# Revit family: Serene_T&T_Window_F_Standard
name_source: partatom
category: Windows
revit_build: Autodesk Revit 2014 (Build: 20130308_1515(x64)
units: mm (PartAtom-declared; Revit-internal decimal feet)

## types (12) — shared parameters
Area Glazing Sash = 0.43 m²
Centered In Wall = Yes
Custom Sash Height = 1122 mm  [stored 3.6811 ft]
Custom Sash Width = 522 mm  [stored 1.7126 ft]
DG Gasket Finish = Double Glazing Gasket Material
DG Gasket Tickness = 12 mm  [stored 0.0393701 ft]
DG Thickness Calc = 4 mm  [stored 0.0131234 ft]
Default Sill Height = 800 mm  [stored 2.62467 ft]
Description = Tilt and turn window, Type F
Fixed Panel Bottom Width = 510 mm
Frame Thickness = 52 mm
Frame Width = 62 mm  [stored 0.203412 ft]
Length Transom = 510 mm
Limit Fixed Panel Height Max = 1800 mm  [stored 5.90551 ft]
Limit Fixed Panel Height Min = 200 mm  [stored 0.656168 ft]
Limit Fixed Panel Width Max = 1800 mm  [stored 5.90551 ft]
Limit Fixed Panel Width Min = 200 mm  [stored 0.656168 ft]
Limit Sash Height Max = 1500 mm  [stored 4.92126 ft]
Limit Sash Height Min = 300 mm  [stored 0.984252 ft]
Limit Sash Width Max = 700 mm  [stored 2.29659 ft]
Limit Sash Width Min = 300 mm  [stored 0.984252 ft]
Limit Window Height Max = 1880 mm  [stored 6.16798 ft]
Limit Window Height Min = 1430 mm
Limit Window Width Max = 2979 mm
Limit Window Width Min = 1379 mm
Manufacturer = Crealco
Max System DG One Piece Thickness = 4 mm  [stored 0.0131234 ft]
Max System DG Unit Thickness = 20 mm  [stored 0.0656168 ft]
Model = Serene
Mullion Side Spacing = 528 mm  [stored 1.73228 ft]
Sash Edge Gap = 34 mm
Sash Frame Gasket = 3 mm  [stored 0.00984252 ft]
Sash Height = 1122 mm  [stored 3.6811 ft]
Sash Overlap = 28 mm  [stored 0.0918635 ft]
Sash Width = 522 mm  [stored 1.7126 ft]
URL = http://www.crealco.co.za
Wall Closure = By host
zero-valued in all types: Custom Window Exterior Offset

## per-type parameters (varying)
- 52TT-1815SS-1000Pa: Area Glazing Fixed Panel Bottom=0.13 m²; Area Glazing Fixed Panel Middle=0.84 m²; Clearvue Insulated LowE SHGC Value=0.441; Clearvue Insulated LowE U Value=3.78; Clearvue Insulated SHGC Value=0.484; Clearvue Insulated U Value=4.24; Clearvue SHGC Value=0.549; Clearvue U Value=6.2; Custom Windload=1000 mm  [stored 3.28084 ft]; Custom Window Height=1490 mm  [stored 4.88845 ft]; Custom Window Width=1790 mm  [stored 5.8727 ft]; Energy Advantage SHGC Value=0.493; Energy Advantage U Value=5.33; Fixed Panel Bottom Height=260 mm; Fixed Panel Middle Height=1410 mm  [stored 4.62598 ft]; Fixed Panel Middle Width=611 mm; Heavy Duty Mullion=No; Height=1490 mm  [stored 4.88845 ft]; Intruderprufe LowE SHGC Value=0.451; Intruderprufe LowE U Value=4.53; Intruderprufe SHGC Value=0.509; Intruderprufe U Value=6.09; Length Decorative Mullion=1490 mm  [stored 4.88845 ft]; Length Mullion=1410 mm  [stored 4.62598 ft]; Max Pane Area=0.84 m²; Standard Mullion=Yes; Width=1790 mm  [stored 5.8727 ft]; Windload Design=1000 mm  [stored 3.28084 ft]
- 52TT-1815SS-1500Pa: Area Glazing Fixed Panel Bottom=0.13 m²; Area Glazing Fixed Panel Middle=0.84 m²; Clearvue Insulated LowE SHGC Value=0.441; Clearvue Insulated LowE U Value=3.78; Clearvue Insulated SHGC Value=0.484; Clearvue Insulated U Value=4.24; Clearvue SHGC Value=0.549; Clearvue U Value=6.2; Custom Windload=1500 mm  [stored 4.92126 ft]; Custom Window Height=1490 mm  [stored 4.88845 ft]; Custom Window Width=1790 mm  [stored 5.8727 ft]; Energy Advantage SHGC Value=0.493; Energy Advantage U Value=5.33; Fixed Panel Bottom Height=260 mm; Fixed Panel Middle Height=1410 mm  [stored 4.62598 ft]; Fixed Panel Middle Width=611 mm; Heavy Duty Mullion=Yes; Height=1490 mm  [stored 4.88845 ft]; Intruderprufe LowE SHGC Value=0.451; Intruderprufe LowE U Value=4.53; Intruderprufe SHGC Value=0.509; Intruderprufe U Value=6.09; Length Decorative Mullion=1490 mm  [stored 4.88845 ft]; Length Mullion=1410 mm  [stored 4.62598 ft]; Max Pane Area=0.84 m²; Standard Mullion=No; Width=1790 mm  [stored 5.8727 ft]; Windload Design=1500 mm  [stored 4.92126 ft]
- 52TT-1815SS-2000Pa: Area Glazing Fixed Panel Bottom=0.13 m²; Area Glazing Fixed Panel Middle=0.84 m²; Clearvue Insulated LowE SHGC Value=0.441; Clearvue Insulated LowE U Value=3.78; Clearvue Insulated SHGC Value=0.484; Clearvue Insulated U Value=4.24; Clearvue SHGC Value=0.549; Clearvue U Value=6.2; Custom Windload=2000 mm  [stored 6.56168 ft]; Custom Window Height=1490 mm  [stored 4.88845 ft]; Custom Window Width=1790 mm  [stored 5.8727 ft]; Energy Advantage SHGC Value=0.493; Energy Advantage U Value=5.33; Fixed Panel Bottom Height=260 mm; Fixed Panel Middle Height=1410 mm  [stored 4.62598 ft]; Fixed Panel Middle Width=611 mm; Heavy Duty Mullion=Yes; Height=1490 mm  [stored 4.88845 ft]; Intruderprufe LowE SHGC Value=0.451; Intruderprufe LowE U Value=4.53; Intruderprufe SHGC Value=0.509; Intruderprufe U Value=6.09; Length Decorative Mullion=1490 mm  [stored 4.88845 ft]; Length Mullion=1410 mm  [stored 4.62598 ft]; Max Pane Area=0.84 m²; Standard Mullion=No; Width=1790 mm  [stored 5.8727 ft]; Windload Design=2000 mm  [stored 6.56168 ft]
- 52TT-2415SS-1000Pa: Area Glazing Fixed Panel Bottom=0.13 m²; Area Glazing Fixed Panel Middle=1.68 m²; Clearvue Insulated LowE SHGC Value=0.487; Clearvue Insulated LowE U Value=3.42; Clearvue Insulated SHGC Value=0.535; Clearvue Insulated U Value=3.95; Clearvue SHGC Value=0; Clearvue U Value=7.9; Custom Windload=1000 mm  [stored 3.28084 ft]; Custom Window Height=1490 mm  [stored 4.88845 ft]; Custom Window Width=2390 mm  [stored 7.84121 ft]; Energy Advantage SHGC Value=0; Energy Advantage U Value=7.9; Fixed Panel Bottom Height=260 mm; Fixed Panel Middle Height=1410 mm  [stored 4.62598 ft]; Fixed Panel Middle Width=1211 mm; Heavy Duty Mullion=No; Height=1490 mm  [stored 4.88845 ft]; Intruderprufe LowE SHGC Value=0.497; Intruderprufe LowE U Value=4.46; Intruderprufe SHGC Value=0.561; Intruderprufe U Value=6; Length Decorative Mullion=1490 mm  [stored 4.88845 ft]; Length Mullion=1410 mm  [stored 4.62598 ft]; Max Pane Area=1.68 m²; Standard Mullion=Yes; Width=2390 mm  [stored 7.84121 ft]; Windload Design=1000 mm  [stored 3.28084 ft]
- 52TT-2415SS-1500Pa: Area Glazing Fixed Panel Bottom=0.13 m²; Area Glazing Fixed Panel Middle=1.68 m²; Clearvue Insulated LowE SHGC Value=0.487; Clearvue Insulated LowE U Value=3.42; Clearvue Insulated SHGC Value=0.535; Clearvue Insulated U Value=3.95; Clearvue SHGC Value=0; Clearvue U Value=7.9; Custom Windload=1500 mm  [stored 4.92126 ft]; Custom Window Height=1490 mm  [stored 4.88845 ft]; Custom Window Width=2390 mm  [stored 7.84121 ft]; Energy Advantage SHGC Value=0; Energy Advantage U Value=7.9; Fixed Panel Bottom Height=260 mm; Fixed Panel Middle Height=1410 mm  [stored 4.62598 ft]; Fixed Panel Middle Width=1211 mm; Heavy Duty Mullion=Yes; Height=1490 mm  [stored 4.88845 ft]; Intruderprufe LowE SHGC Value=0.497; Intruderprufe LowE U Value=4.46; Intruderprufe SHGC Value=0.561; Intruderprufe U Value=6; Length Decorative Mullion=1490 mm  [stored 4.88845 ft]; Length Mullion=1410 mm  [stored 4.62598 ft]; Max Pane Area=1.68 m²; Standard Mullion=No; Width=2390 mm  [stored 7.84121 ft]; Windload Design=1500 mm  [stored 4.92126 ft]
- 52TT-2415SS-2000Pa: Area Glazing Fixed Panel Bottom=0.13 m²; Area Glazing Fixed Panel Middle=1.68 m²; Clearvue Insulated LowE SHGC Value=0.487; Clearvue Insulated LowE U Value=3.42; Clearvue Insulated SHGC Value=0.535; Clearvue Insulated U Value=3.95; Clearvue SHGC Value=0; Clearvue U Value=7.9; Custom Windload=2000 mm  [stored 6.56168 ft]; Custom Window Height=1490 mm  [stored 4.88845 ft]; Custom Window Width=2390 mm  [stored 7.84121 ft]; Energy Advantage SHGC Value=0; Energy Advantage U Value=7.9; Fixed Panel Bottom Height=260 mm; Fixed Panel Middle Height=1410 mm  [stored 4.62598 ft]; Fixed Panel Middle Width=1211 mm; Heavy Duty Mullion=Yes; Height=1490 mm  [stored 4.88845 ft]; Intruderprufe LowE SHGC Value=0.497; Intruderprufe LowE U Value=4.46; Intruderprufe SHGC Value=0.561; Intruderprufe U Value=6; Length Decorative Mullion=1490 mm  [stored 4.88845 ft]; Length Mullion=1410 mm  [stored 4.62598 ft]; Max Pane Area=1.68 m²; Standard Mullion=No; Width=2390 mm  [stored 7.84121 ft]; Windload Design=2000 mm  [stored 6.56168 ft]
- 52TT-1818SS-1000Pa: Area Glazing Fixed Panel Bottom=0.27 m²; Area Glazing Fixed Panel Middle=1.02 m²; Clearvue Insulated LowE SHGC Value=0.459; Clearvue Insulated LowE U Value=3.64; Clearvue Insulated SHGC Value=0.504; Clearvue Insulated U Value=4.12; Clearvue SHGC Value=0.573; Clearvue U Value=6.16; Custom Windload=1000 mm  [stored 3.28084 ft]; Custom Window Height=1790 mm  [stored 5.8727 ft]; Custom Window Width=1790 mm  [stored 5.8727 ft]; Energy Advantage SHGC Value=0.514; Energy Advantage U Value=5.23; Fixed Panel Bottom Height=560 mm; Fixed Panel Middle Height=1710 mm  [stored 5.61024 ft]; Fixed Panel Middle Width=611 mm; Heavy Duty Mullion=Yes; Height=1790 mm  [stored 5.8727 ft]; Intruderprufe LowE SHGC Value=0.47; Intruderprufe LowE U Value=4.5; Intruderprufe SHGC Value=0.53; Intruderprufe U Value=6.05; Length Decorative Mullion=1790 mm  [stored 5.8727 ft]; Length Mullion=1710 mm  [stored 5.61024 ft]; Max Pane Area=1.02 m²; Standard Mullion=No; Width=1790 mm  [stored 5.8727 ft]; Windload Design=1000 mm  [stored 3.28084 ft]
- 52TT-1818SS-1500Pa: Area Glazing Fixed Panel Bottom=0.27 m²; Area Glazing Fixed Panel Middle=1.02 m²; Clearvue Insulated LowE SHGC Value=0.459; Clearvue Insulated LowE U Value=3.64; Clearvue Insulated SHGC Value=0.504; Clearvue Insulated U Value=4.12; Clearvue SHGC Value=0.573; Clearvue U Value=6.16; Custom Windload=1500 mm  [stored 4.92126 ft]; Custom Window Height=1790 mm  [stored 5.8727 ft]; Custom Window Width=1790 mm  [stored 5.8727 ft]; Energy Advantage SHGC Value=0.514; Energy Advantage U Value=5.23; Fixed Panel Bottom Height=560 mm; Fixed Panel Middle Height=1710 mm  [stored 5.61024 ft]; Fixed Panel Middle Width=611 mm; Heavy Duty Mullion=Yes; Height=1790 mm  [stored 5.8727 ft]; Intruderprufe LowE SHGC Value=0.47; Intruderprufe LowE U Value=4.5; Intruderprufe SHGC Value=0.53; Intruderprufe U Value=6.05; Length Decorative Mullion=1790 mm  [stored 5.8727 ft]; Length Mullion=1710 mm  [stored 5.61024 ft]; Max Pane Area=1.02 m²; Standard Mullion=No; Width=1790 mm  [stored 5.8727 ft]; Windload Design=1500 mm  [stored 4.92126 ft]
- 52TT-1818SS-2000Pa: Area Glazing Fixed Panel Bottom=0.27 m²; Area Glazing Fixed Panel Middle=1.02 m²; Clearvue Insulated LowE SHGC Value=0.459; Clearvue Insulated LowE U Value=3.64; Clearvue Insulated SHGC Value=0.504; Clearvue Insulated U Value=4.12; Clearvue SHGC Value=0.573; Clearvue U Value=6.16; Custom Windload=2000 mm  [stored 6.56168 ft]; Custom Window Height=1790 mm  [stored 5.8727 ft]; Custom Window Width=1790 mm  [stored 5.8727 ft]; Energy Advantage SHGC Value=0.514; Energy Advantage U Value=5.23; Fixed Panel Bottom Height=560 mm; Fixed Panel Middle Height=1710 mm  [stored 5.61024 ft]; Fixed Panel Middle Width=611 mm; Heavy Duty Mullion=Yes; Height=1790 mm  [stored 5.8727 ft]; Intruderprufe LowE SHGC Value=0.47; Intruderprufe LowE U Value=4.5; Intruderprufe SHGC Value=0.53; Intruderprufe U Value=6.05; Length Decorative Mullion=1790 mm  [stored 5.8727 ft]; Length Mullion=1710 mm  [stored 5.61024 ft]; Max Pane Area=1.02 m²; Standard Mullion=No; Width=1790 mm  [stored 5.8727 ft]; Windload Design=2000 mm  [stored 6.56168 ft]
- 52TT-2418SS-1000Pa: Area Glazing Fixed Panel Bottom=0.27 m²; Area Glazing Fixed Panel Middle=2.04 m²; Clearvue Insulated LowE SHGC Value=0.503; Clearvue Insulated LowE U Value=3.29; Clearvue Insulated SHGC Value=0.552; Clearvue Insulated U Value=3.84; Clearvue SHGC Value=0; Clearvue U Value=7.9; Custom Windload=1000 mm  [stored 3.28084 ft]; Custom Window Height=1790 mm  [stored 5.8727 ft]; Custom Window Width=2390 mm  [stored 7.84121 ft]; Energy Advantage SHGC Value=0; Energy Advantage U Value=7.9; Fixed Panel Bottom Height=560 mm; Fixed Panel Middle Height=1710 mm  [stored 5.61024 ft]; Fixed Panel Middle Width=1211 mm; Heavy Duty Mullion=Yes; Height=1790 mm  [stored 5.8727 ft]; Intruderprufe LowE SHGC Value=0.514; Intruderprufe LowE U Value=4.43; Intruderprufe SHGC Value=0.58; Intruderprufe U Value=5.96; Length Decorative Mullion=1790 mm  [stored 5.8727 ft]; Length Mullion=1710 mm  [stored 5.61024 ft]; Max Pane Area=2.04 m²; Standard Mullion=No; Width=2390 mm  [stored 7.84121 ft]; Windload Design=1000 mm  [stored 3.28084 ft]
- 52TT-2418SS-1500Pa: Area Glazing Fixed Panel Bottom=0.27 m²; Area Glazing Fixed Panel Middle=2.04 m²; Clearvue Insulated LowE SHGC Value=0.503; Clearvue Insulated LowE U Value=3.29; Clearvue Insulated SHGC Value=0.552; Clearvue Insulated U Value=3.84; Clearvue SHGC Value=0; Clearvue U Value=7.9; Custom Windload=1500 mm  [stored 4.92126 ft]; Custom Window Height=1790 mm  [stored 5.8727 ft]; Custom Window Width=2390 mm  [stored 7.84121 ft]; Energy Advantage SHGC Value=0; Energy Advantage U Value=7.9; Fixed Panel Bottom Height=560 mm; Fixed Panel Middle Height=1710 mm  [stored 5.61024 ft]; Fixed Panel Middle Width=1211 mm; Heavy Duty Mullion=Yes; Height=1790 mm  [stored 5.8727 ft]; Intruderprufe LowE SHGC Value=0.514; Intruderprufe LowE U Value=4.43; Intruderprufe SHGC Value=0.58; Intruderprufe U Value=5.96; Length Decorative Mullion=1790 mm  [stored 5.8727 ft]; Length Mullion=1710 mm  [stored 5.61024 ft]; Max Pane Area=2.04 m²; Standard Mullion=No; Width=2390 mm  [stored 7.84121 ft]; Windload Design=1500 mm  [stored 4.92126 ft]
- 52TT-2418SS-2000Pa: Area Glazing Fixed Panel Bottom=0.27 m²; Area Glazing Fixed Panel Middle=2.04 m²; Clearvue Insulated LowE SHGC Value=0.503; Clearvue Insulated LowE U Value=3.29; Clearvue Insulated SHGC Value=0.552; Clearvue Insulated U Value=3.84; Clearvue SHGC Value=0; Clearvue U Value=7.9; Custom Windload=2000 mm  [stored 6.56168 ft]; Custom Window Height=1790 mm  [stored 5.8727 ft]; Custom Window Width=2390 mm  [stored 7.84121 ft]; Energy Advantage SHGC Value=0; Energy Advantage U Value=7.9; Fixed Panel Bottom Height=560 mm; Fixed Panel Middle Height=1710 mm  [stored 5.61024 ft]; Fixed Panel Middle Width=1211 mm; Heavy Duty Mullion=Yes; Height=1790 mm  [stored 5.8727 ft]; Intruderprufe LowE SHGC Value=0.514; Intruderprufe LowE U Value=4.43; Intruderprufe SHGC Value=0.58; Intruderprufe U Value=5.96; Length Decorative Mullion=1790 mm  [stored 5.8727 ft]; Length Mullion=1710 mm  [stored 5.61024 ft]; Max Pane Area=2.04 m²; Standard Mullion=No; Width=2390 mm  [stored 7.84121 ft]; Windload Design=2000 mm  [stored 6.56168 ft]

note: [stored X ft] marks values corroborated as IEEE doubles in the binary element streams (Revit-internal decimal feet)

## geometry (parser evidence)
native form markers: Sweep x43
no freeform markers — native parametric forms only
